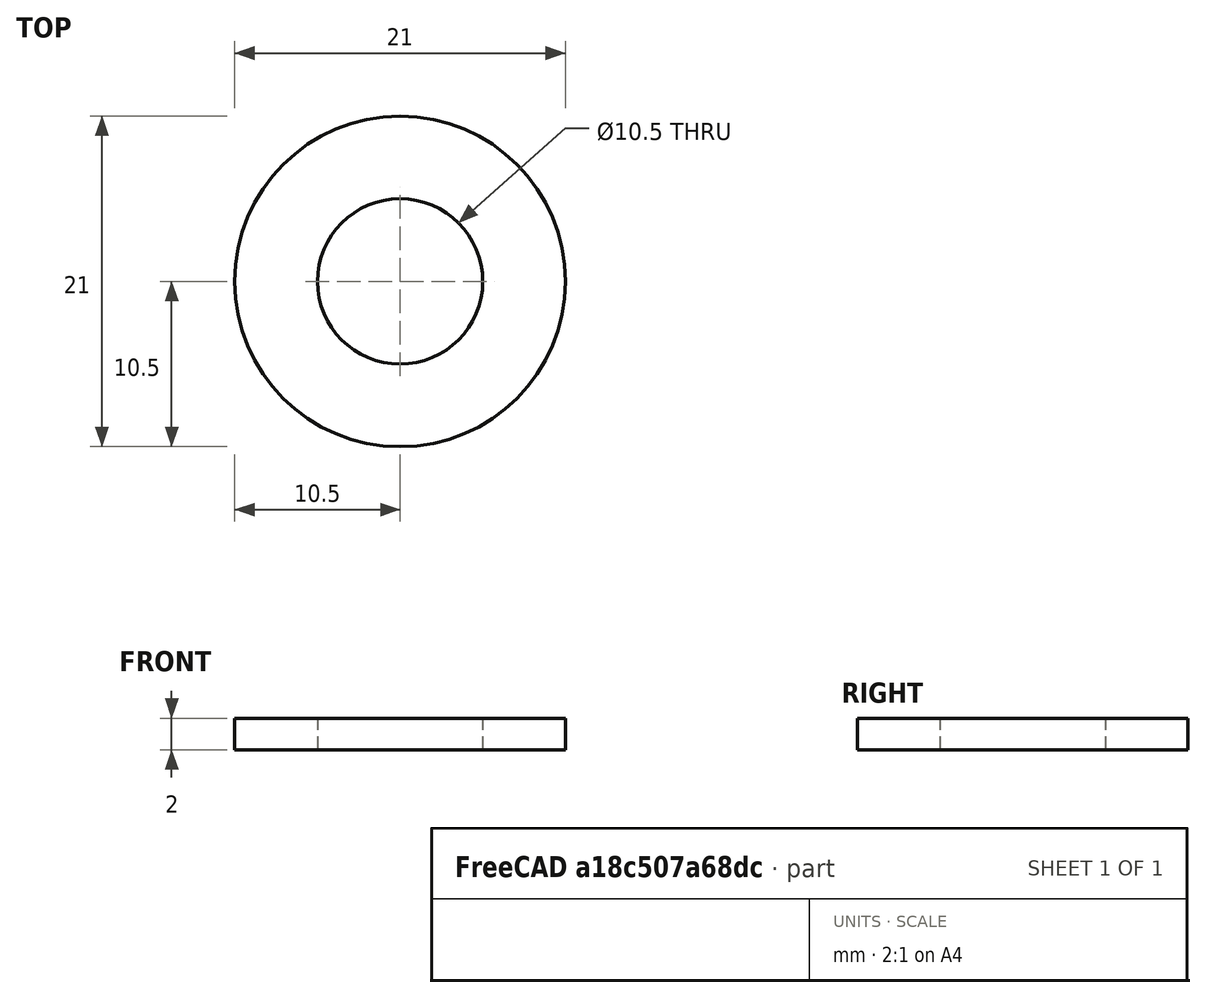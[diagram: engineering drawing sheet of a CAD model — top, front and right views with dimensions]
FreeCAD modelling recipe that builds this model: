
FCSTD DOCUMENT  (FreeCAD 0.14R3700 (Git))
Label: Scheibe DIN 125 - A 10,5
License: CC-BY 3.0
LicenseURL: http://creativecommons.org/licenses/by/3.0/
objects: Sketcher::SketchObject×1, PartDesign::Revolution×1, Part::Feature×1
note: 4 computed .brp shape members not serialized (recipe doc carries the construction recipe); baked Part::Feature solids carry a one-line shape summary decoded from their .brp

FEATURE [Sketcher::SketchObject] Sketch
  Placement = pos=(0,0,0) rot=(0.57735,0.57735,0.57735;2.0944rad)
  sketch-geometry (4):
    g0: LineSegment StartX=5.25 StartY=0 StartZ=0 EndX=10.5 EndY=0 EndZ=0
    g1: LineSegment StartX=10.5 StartY=0 StartZ=0 EndX=10.5 EndY=2 EndZ=0
    g2: LineSegment StartX=10.5 StartY=2 StartZ=0 EndX=5.25 EndY=2 EndZ=0
    g3: LineSegment StartX=5.25 StartY=2 StartZ=0 EndX=5.25 EndY=0 EndZ=0
  constraints (12):
    c: Coincident(g0,g1)
    c: Coincident(g1,g2)
    c: Coincident(g2,g3)
    c: Coincident(g3,g0)
    c: Horizontal(g0)
    c: Horizontal(g2)
    c: Vertical(g1)
    c: Vertical(g3)
    c: PointOnObject(g0,g-1)
    c: DistanceY(g1) = 2
    c: DistanceX(g-1,g2) = 5.25
    c: DistanceX(g-1,g1) = 10.5
FEATURE [PartDesign::Revolution] Revolution  label="Scheibe DIN 125 - A 10,5 #"
  Angle = 360
  Axis = (0,0,1)
  Base = (0,0,0)
  Placement = pos=(0,0,0) rot=(0.57735,0.57735,0.57735;2.0944rad)
  ReferenceAxis = -> Sketch [V_Axis]
  Reversed = true
  Sketch = -> Sketch
FEATURE [Part::Feature] Revolution001  label="Scheibe DIN 125 - A 10,5 #001"
  Placement = pos=(0,0,0) rot=(0.57735,0.57735,0.57735;2.0944rad)
  shape: bbox 21 x 21 x 2 mm, 4 faces (baked)
